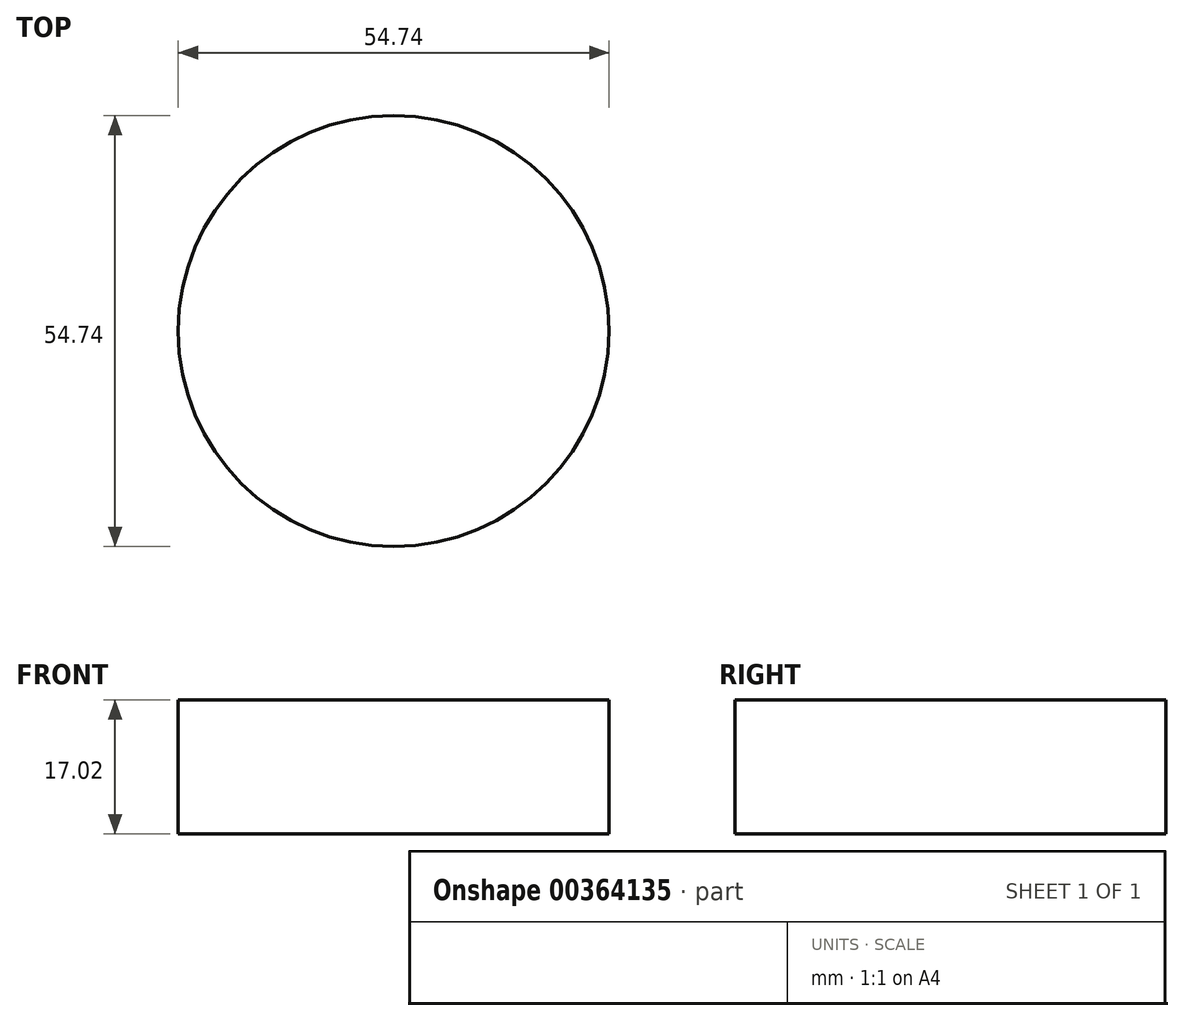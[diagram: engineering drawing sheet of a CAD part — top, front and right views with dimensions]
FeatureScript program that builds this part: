
annotation { "Feature Type Name" : "Feature", "Feature Type Description" : "" }
export const myFeature = defineFeature(function(context is Context, id is Id, definition is map)
    precondition{}
    {
        {
            var Q0;
            Q0=qCreatedBy(makeId("Top.planeOp"),FACE);
            var sketch = newSketch(context, id + "F0", { "sketchPlane" : qUnion([Q0])});
            skCircle(sketch, "E0", {"center": v(0, 0) * mm, "radius": 27.37 * mm});
            skSolve(sketch);
        }
        {
            var Q0;
            Q0=sQuery(id+"F0.wireOp",EDGE,"E0");
            extrude(context, id + "F1", {"bodyType" : ToolBodyType.SURFACE, "surfaceEntities" : qUnion([Q0]), "depth" : 17.02 * mm});
        }
    });
